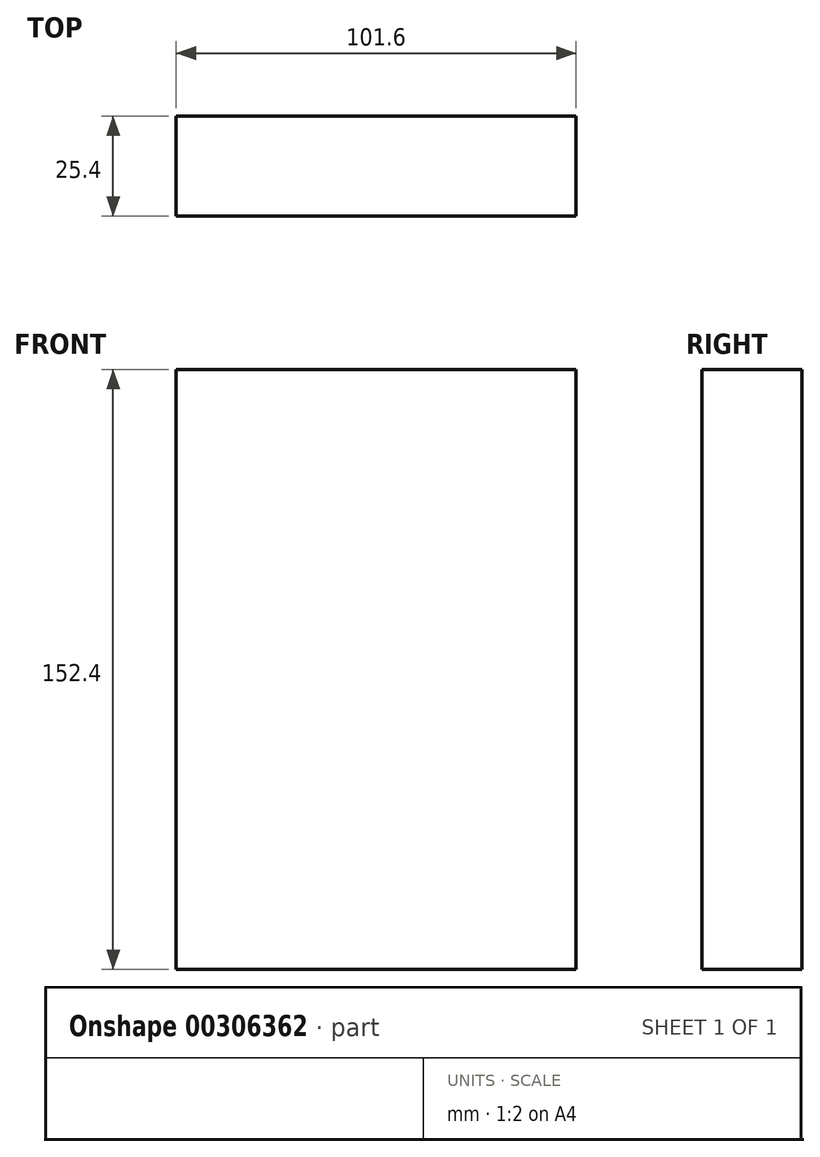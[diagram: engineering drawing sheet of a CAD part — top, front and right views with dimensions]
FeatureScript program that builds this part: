
annotation { "Feature Type Name" : "Feature", "Feature Type Description" : "" }
export const myFeature = defineFeature(function(context is Context, id is Id, definition is map)
    precondition{}
    {
        {
            var Q0;
            Q0=qCreatedBy(makeId("Front.planeOp"),FACE);
            var sketch = newSketch(context, id + "F0", { "sketchPlane" : qUnion([Q0])});
            skLineSegment(sketch, "E0.bottom", {"start": v(-50.8, 76.2) * mm, "end": v(50.8, 76.2) * mm});
            skLineSegment(sketch, "E0.top", {"start": v(-50.8, -76.2) * mm, "end": v(50.8, -76.2) * mm});
            skLineSegment(sketch, "E0.left", {"start": v(-50.8, 76.2) * mm, "end": v(-50.8, -76.2) * mm});
            skLineSegment(sketch, "E0.right", {"start": v(50.8, 76.2) * mm, "end": v(50.8, -76.2) * mm});
            skPoint(sketch, "E0.middle", {"position": v(0, 0) * mm});
            skSolve(sketch);
        }
        {
            var Q0;
            Q0=makeQuery(id+"F0.imprint","IMPRINT",FACE,{"disambiguationData":[TD([[makeQuery(id+"F0.imprint","IMPRINT",EDGE,{"derivedFrom":sQuery(id+"F0.wireOp",EDGE,"E0.bottom")}),-1.0]])]});
            extrude(context, id + "F1", {"entities" : qUnion([Q0]), "depth" : 25.4 * mm});
        }
    });
